# Revit family: DC_Rheem_PLM_Raypak_B0350HWT
name_source: partatom
category: Mechanical Equipment
units: mm (PartAtom-declared; Revit-internal decimal feet)

## family parameters
Cut with Voids When Loaded = No
Host = Face
Part Type = Normal
Room Calculation Point = No
Round Connector Dimension = Use Radius
Shared = No

## types (4) — shared parameters
BoxHeight_ANZRS = 985 mm
ColdWaterConnectionDistance_ANZRS = 215 mm  [stored 0.705381 ft]
ColdWaterInletDiameter_ANZRS = 40 mm
ColdWaterInletRadius_ANZRS = 20 mm  [stored 0.0656168 ft]
ConnectionHeight_ANZRS = 700 mm
FootingOffsetDistanceRight_ANZRS = 105 mm
FootingOffsetDistance_ANZRS = 30 mm  [stored 0.0984252 ft]
FootingWidth_ANZRS = 50 mm  [stored 0.164042 ft]
GasConnectionDistance_ANZRS = 105 mm
GasInletHeight_ANZRS = 370 mm
Height_ANZRS = 2035 mm  [stored 6.67651 ft]
HotWaterConnectionDistance_ANZRS = 170 mm
HotWaterOutletDiameter_ANZRS = 40 mm
HotWaterOutletRadius_ANZRS = 20 mm  [stored 0.0656168 ft]
Length_ANZRS = 675 mm  [stored 2.21457 ft]
LipHeight_ANZRS = 935 mm
Manufacturer = Raypak
PRVDiameter_ANZRS = 30 mm  [stored 0.0984252 ft]
PRVDistance_ANZRS = 210 mm  [stored 0.688976 ft]
PRVRadius_ANZRS = 15 mm  [stored 0.0492126 ft]
Stainless Steel = Raypak - Grey Powder Coated Steel
TopDiameter_ANZRS = 225 mm
URL = http://www.rheem.com.au
Width_ANZRS = 655 mm
zero-valued in all types: Default Elevation

## per-type parameters (varying)
| type | GasInletDiameter_ANZRS | GasInletRadius_ANZRS | Model | Type Comments |
| Raypak - Gas Water Heater- Outdoor - 343 MJ/h  Natural gas, modulating gas control | 25 mm  [stored 0.082021 ft] | 13 mm | B0350NCM/HWT | Recovery 1312L/h @ 50oC rise |
| Raypak - Gas Water Heater- Outdoor - 343 MJ/h  Natural gas, On/Off gas control | 20 mm  [stored 0.0656168 ft] | 10 mm  [stored 0.0328084 ft] | B0350NCO/HWT | Recovery 1312L/h @ 50oC rise |
| Raypak - Gas Water Heater- Outdoor - 323 MJ/h  Propane gas, modulating gas control | 20 mm  [stored 0.0656168 ft] | 10 mm  [stored 0.0328084 ft] | B0350PCM/HWT | Recovery 1238L/h @ 50oC rise |
| Raypak - Gas Water Heater- Outdoor - 323 MJ/h  Propane gas, On/Off gas control | 20 mm  [stored 0.0656168 ft] | 10 mm  [stored 0.0328084 ft] | B0350PCO/HWT | Recovery 1238L/h @ 50oC rise |

note: column(s) folded — value = type name in every type: Description

note: [stored X ft] marks values corroborated as IEEE doubles in the binary element streams (Revit-internal decimal feet)

## geometry (parser evidence)
native form markers: Blend x6, Sweep x2
no freeform markers — native parametric forms only
